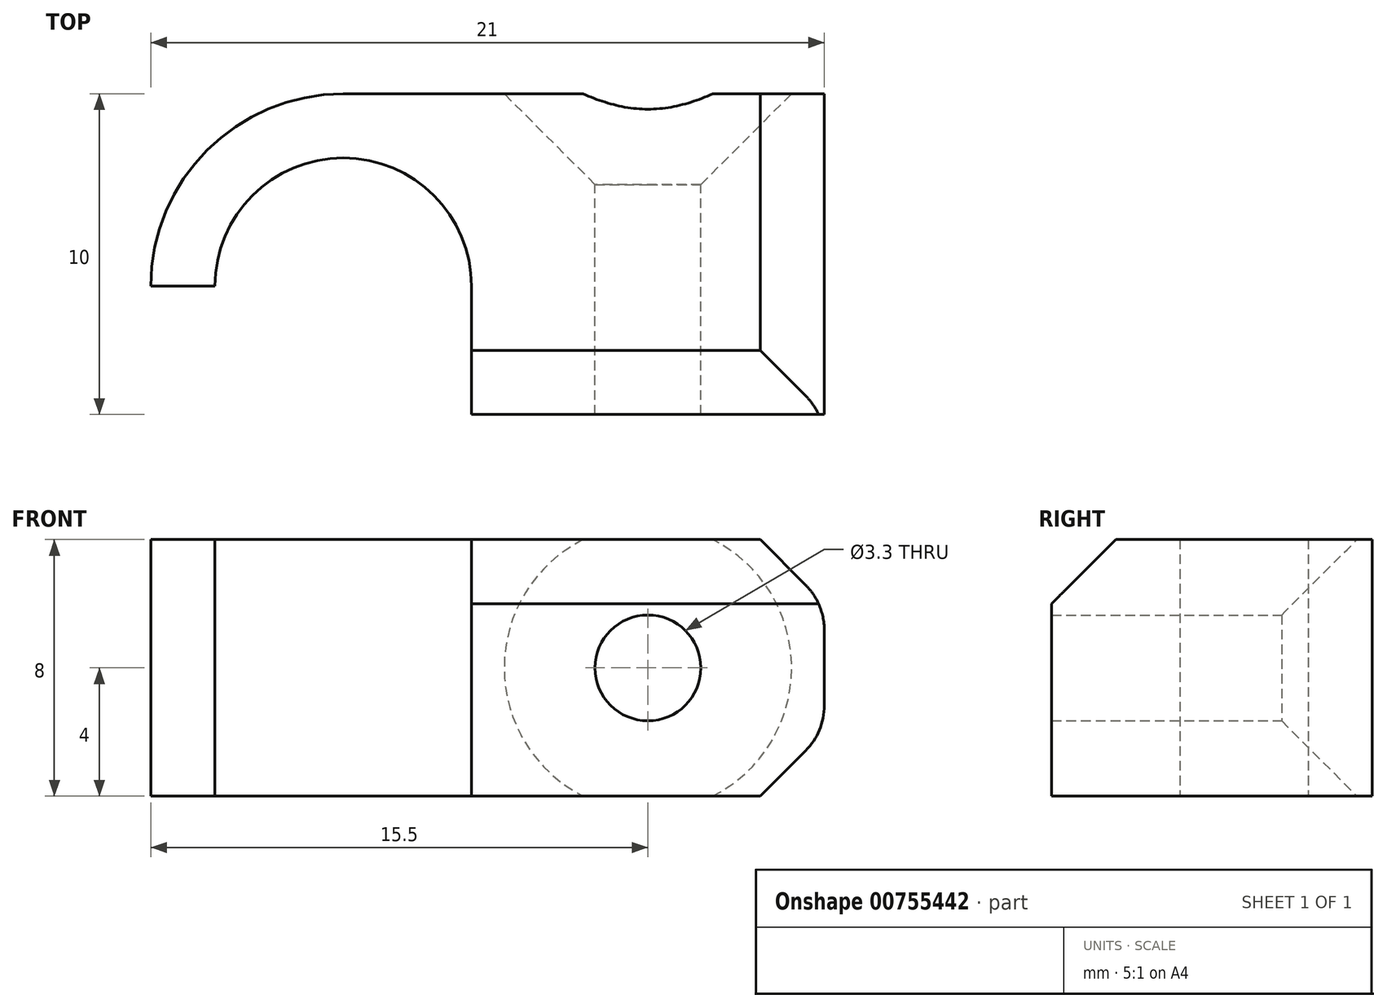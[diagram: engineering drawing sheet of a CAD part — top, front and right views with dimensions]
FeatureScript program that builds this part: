
annotation { "Feature Type Name" : "Feature", "Feature Type Description" : "" }
export const myFeature = defineFeature(function(context is Context, id is Id, definition is map)
    precondition{}
    {
        {
            var Q0;
            Q0=qCreatedBy(makeId("Top.planeOp"),FACE);
            var sketch = newSketch(context, id + "F0", { "sketchPlane" : qUnion([Q0])});
            skArc(sketch, "E0", {"start": v(4, 0) * mm, "mid": v(0, 4) * mm, "end": v(-4, 0) * mm});
            skArc(sketch, "E1.0", {"start": v(0, 6) * mm, "mid": v(-4.24, 4.24) * mm, "end": v(-6, 0) * mm});
            skLineSegment(sketch, "E2", {"start": v(0, 6) * mm, "end": v(15, 6) * mm});
            skLineSegment(sketch, "E3", {"start": v(15, 6) * mm, "end": v(15, -4) * mm});
            skLineSegment(sketch, "E4", {"start": v(4, -4) * mm, "end": v(15, -4) * mm});
            skLineSegment(sketch, "E5", {"start": v(-6, 0) * mm, "end": v(-4, 0) * mm});
            skLineSegment(sketch, "E6", {"start": v(4, 0) * mm, "end": v(4, -4) * mm});
            skPoint(sketch, "E7.orphan", {"position": v(0, -4) * mm});
            skSolve(sketch);
        }
        {
            var Q0;
            Q0=makeQuery(id+"F0.imprint","IMPRINT",FACE,{"disambiguationData":[TD([[makeQuery(id+"F0.imprint","IMPRINT",EDGE,{"derivedFrom":sQuery(id+"F0.wireOp",EDGE,"E0")}),-1.0]])]});
            extrude(context, id + "F1", {"entities" : qUnion([Q0]), "endBound" : BoundingType.SYMMETRIC, "depth" : 8 * mm, "offsetDistance" : 25 * mm});
        }
        {
            var Q0;
            Q0=makeQuery(id+"F1.opExtrude","SWEPT_FACE",FACE,{"disambiguationData":[OSD([sQuery(id+"F0.wireOp",EDGE,"E2")])]});
            var sketch = newSketch(context, id + "F2", { "sketchPlane" : qUnion([Q0])});
            skLineSegment(sketch, "E8", {"start": v(-15, 4) * mm, "end": v(-4, -4) * mm, "construction": true});
            skPoint(sketch, "E9", {"position": v(-9.5, 0) * mm});
            skSolve(sketch);
        }
        {
            var Q0;
            Q0=sQuery(id+"F2.wireOp",VERTEX,"E9");
            var Q1;
            Q1=makeQuery(id+"F1.opExtrude","SWEPT_BODY",BODY,{"disambiguationData":[OSD([sQuery(id+"F0.wireOp",EDGE,"E0"),sQuery(id+"F0.wireOp",EDGE,"E1.0"),sQuery(id+"F0.wireOp",EDGE,"E2"),sQuery(id+"F0.wireOp",EDGE,"E3"),sQuery(id+"F0.wireOp",EDGE,"E4"),sQuery(id+"F0.wireOp",EDGE,"E5"),sQuery(id+"F0.wireOp",EDGE,"E6")])]});
            hole(context, id + "F3", {"style" : HoleStyle.C_SINK, "endStyle" : HoleEndStyle.THROUGH, "standardTappedOrClearance" : lookupTablePath({ "standard" : "ISO", "engagement" : "75%", "pitch" : "0.7 mm", "size" : "M4", "type" : "Tapped" }), "standardBlindInLast" : lookupTablePath({ "standard" : "ISO", "engagement" : "75%", "pitch" : "0.7 mm", "size" : "M4", "type" : "Tapped" }), "holeDiameter" : 3.3 * mm, "cSinkDiameter" : 8.96 * mm, "cSinkAngle" : 90 * degree, "majorDiameter" : 4 * mm, "showTappedDepth" : true, "isTappedThrough" : true, "tappedDepth" : 12 * mm, "tapClearance" : 3, "locations" : qUnion([Q0]), "scope" : qUnion([Q1])});
        }
        {
            var Q0;
            Q0=makeQuery(id+"F1.opExtrude","CAP_EDGE",EDGE,{"disambiguationData":[OSD([sQuery(id+"F0.wireOp",EDGE,"E3")])],"isStart":true});
            var Q1;
            Q1=makeQuery(id+"F1.opExtrude","CAP_EDGE",EDGE,{"disambiguationData":[OSD([sQuery(id+"F0.wireOp",EDGE,"E3")])],"isStart":false});
            chamfer(context, id + "F4", {"entities" : qUnion([Q0, Q1]), "width" : 2 * mm, "tangentPropagation" : true});
        }
        {
            var Q0;
            {var subQ0=sQuery(id+"F0.wireOp",EDGE,"E3");Q0=makeQuery(id+"F4.opChamfer","BLEND_EDGE",EDGE,{"blendedFrom":[makeQuery(id+"F1.opExtrude","CAP_EDGE",EDGE,{"disambiguationData":[OSD([subQ0])],"isStart":false}),makeQuery(id+"F1.opExtrude","SWEPT_FACE",FACE,{"disambiguationData":[OSD([subQ0])]})],"blendedInto":[makeQuery(id+"F1.opExtrude","SWEPT_FACE",FACE,{"disambiguationData":[OSD([subQ0])]})]});}
            var Q1;
            {var subQ0=sQuery(id+"F0.wireOp",EDGE,"E3");Q1=makeQuery(id+"F4.opChamfer","BLEND_EDGE",EDGE,{"blendedFrom":[makeQuery(id+"F1.opExtrude","CAP_EDGE",EDGE,{"disambiguationData":[OSD([subQ0])],"isStart":true}),makeQuery(id+"F1.opExtrude","SWEPT_FACE",FACE,{"disambiguationData":[OSD([subQ0])]})],"blendedInto":[makeQuery(id+"F1.opExtrude","SWEPT_FACE",FACE,{"disambiguationData":[OSD([subQ0])]})]});}
            fillet(context, id + "F5", {"entities" : qUnion([Q0, Q1]), "radius" : 2 * mm, "tangentPropagation" : true, "allowEdgeOverflow" : false});
        }
        {
            var Q0;
            Q0=makeQuery(id+"F1.opExtrude","CAP_EDGE",EDGE,{"disambiguationData":[OSD([sQuery(id+"F0.wireOp",EDGE,"E4")])],"isStart":false});
            chamfer(context, id + "F6", {"entities" : qUnion([Q0]), "width" : 2 * mm, "tangentPropagation" : true});
        }
    });
